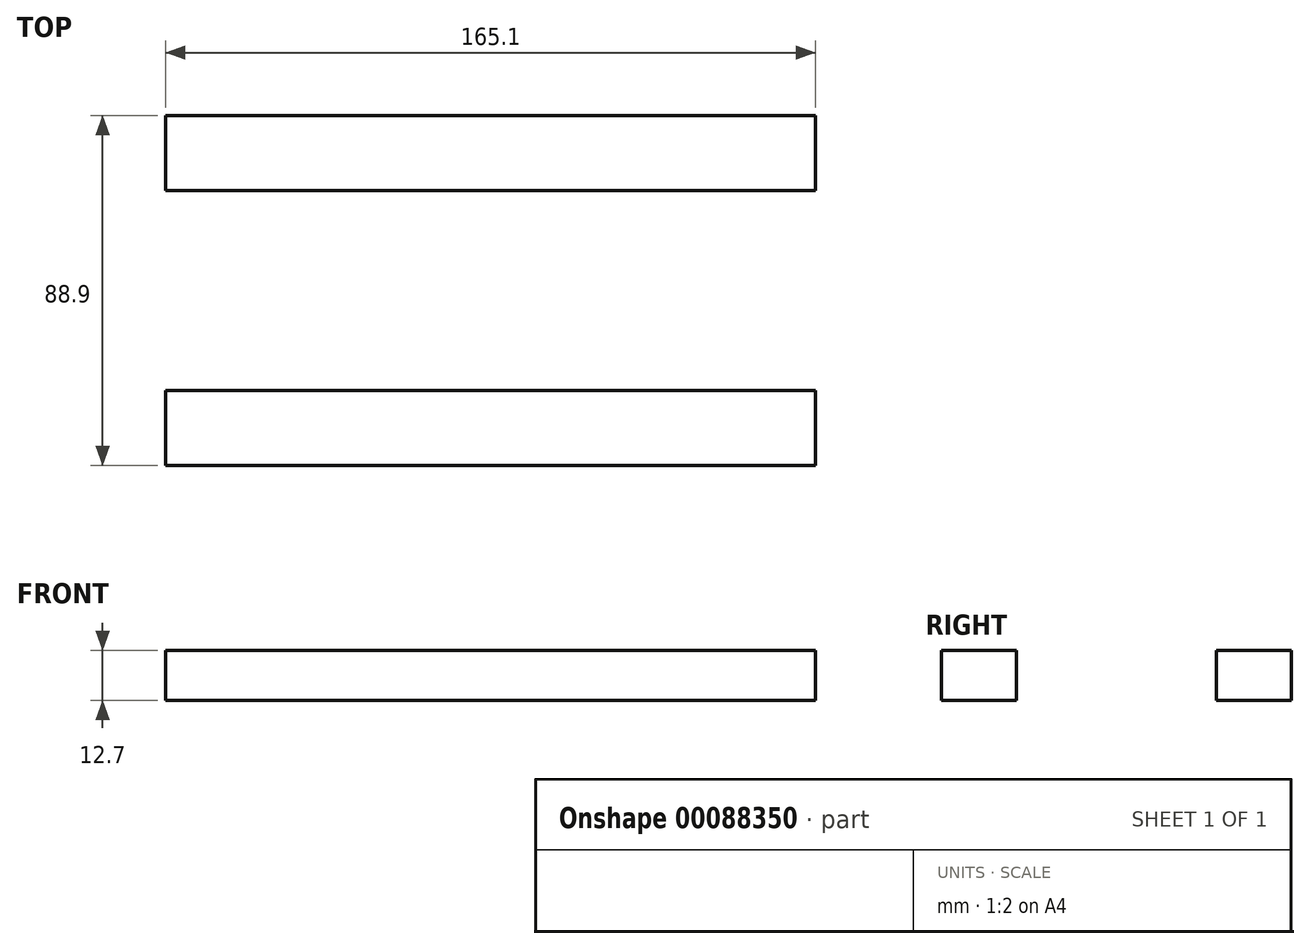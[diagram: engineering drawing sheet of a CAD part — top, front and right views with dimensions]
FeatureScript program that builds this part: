
annotation { "Feature Type Name" : "Feature", "Feature Type Description" : "" }
export const myFeature = defineFeature(function(context is Context, id is Id, definition is map)
    precondition{}
    {
        {
            var Q0;
            Q0=qCreatedBy(makeId("Right.planeOp"),FACE);
            var sketch = newSketch(context, id + "F0", { "sketchPlane" : qUnion([Q0])});
            skLineSegment(sketch, "E0.bottom", {"start": v(0, 0) * mm, "end": v(88.9, 0) * mm});
            skLineSegment(sketch, "E0.top", {"start": v(0, 44.45) * mm, "end": v(88.9, 44.45) * mm});
            skLineSegment(sketch, "E0.left", {"start": v(0, 0) * mm, "end": v(0, 44.45) * mm});
            skLineSegment(sketch, "E0.right", {"start": v(88.9, 0) * mm, "end": v(88.9, 44.45) * mm});
            skLineSegment(sketch, "E1.bottom", {"start": v(0, 44.45) * mm, "end": v(19.05, 44.45) * mm});
            skLineSegment(sketch, "E1.top", {"start": v(0, 31.75) * mm, "end": v(19.05, 31.75) * mm});
            skLineSegment(sketch, "E1.left", {"start": v(0, 44.45) * mm, "end": v(0, 31.75) * mm});
            skLineSegment(sketch, "E1.right", {"start": v(19.05, 44.45) * mm, "end": v(19.05, 31.75) * mm});
            skLineSegment(sketch, "E2.bottom", {"start": v(88.9, 44.45) * mm, "end": v(69.85, 44.45) * mm});
            skLineSegment(sketch, "E2.top", {"start": v(88.9, 31.75) * mm, "end": v(69.85, 31.75) * mm});
            skLineSegment(sketch, "E2.left", {"start": v(88.9, 44.45) * mm, "end": v(88.9, 31.75) * mm});
            skLineSegment(sketch, "E2.right", {"start": v(69.85, 44.45) * mm, "end": v(69.85, 31.75) * mm});
            skLineSegment(sketch, "E3", {"start": v(19.05, 31.75) * mm, "end": v(19.05, 0) * mm});
            skLineSegment(sketch, "E4", {"start": v(19.05, 0) * mm, "end": v(19.05, 12.7) * mm});
            skLineSegment(sketch, "E5", {"start": v(19.05, 12.7) * mm, "end": v(69.85, 12.7) * mm});
            skLineSegment(sketch, "E6", {"start": v(69.85, 12.7) * mm, "end": v(69.85, 31.75) * mm});
            skLineSegment(sketch, "E7", {"start": v(69.85, 0) * mm, "end": v(69.85, 12.7) * mm});
            skSolve(sketch);
        }
        {
            var Q0;
            {var subQ0=sQuery(id+"F0.wireOp",EDGE,"E0.left");Q0=makeQuery(id+"F0.imprint","IMPRINT",FACE,{"disambiguationData":[TD([[makeQuery(id+"F0.imprint","IMPRINT",EDGE,{"derivedFrom":subQ0}),-1.0]])]});}
            var Q1;
            Q1=makeQuery(id+"F0.imprint","IMPRINT",FACE,{"disambiguationData":[TD([[makeQuery(id+"F0.imprint","IMPRINT",EDGE,{"derivedFrom":sQuery(id+"F0.wireOp",EDGE,"E0.top")}),-1.0]])]});
            var Q2;
            {var subQ0=sQuery(id+"F0.wireOp",EDGE,"E0.right");Q2=makeQuery(id+"F0.imprint","IMPRINT",FACE,{"disambiguationData":[TD([[makeQuery(id+"F0.imprint","IMPRINT",EDGE,{"derivedFrom":subQ0}),1.0]])]});}
            extrude(context, id + "F1", {"entities" : qUnion([Q0, Q1, Q2]), "depth" : 165.1 * mm});
        }
        {
            var Q0;
            Q0=makeQuery(id+"F1.opExtrude","SWEPT_FACE",FACE,{"disambiguationData":[OSD([sQuery(id+"F0.wireOp",EDGE,"E0.top")])]});
            var sketch = newSketch(context, id + "F2", { "sketchPlane" : qUnion([Q0])});
            skLineSegment(sketch, "E8", {"start": v(0, 19.05) * mm, "end": v(0, 69.85) * mm});
            skLineSegment(sketch, "E9", {"start": v(0, 69.85) * mm, "end": v(0, 44.45) * mm});
            skLineSegment(sketch, "E10", {"start": v(0, 44.45) * mm, "end": v(35.05, 44.45) * mm});
            skLineSegment(sketch, "E11", {"start": v(35.05, 44.45) * mm, "end": v(130.3, 44.45) * mm});
            skSolve(sketch);
        }
        {
            var Q0;
            Q0=sQuery(id+"F2.wireOp",VERTEX,"E11.end");
            var Q1;
            Q1=sQuery(id+"F2.wireOp",VERTEX,"E11.start");
            var Q2;
            Q2=makeQuery(id+"F1.opExtrude","SWEPT_BODY",BODY,{"disambiguationData":[OSD([sQuery(id+"F0.wireOp",EDGE,"E0.bottom"),sQuery(id+"F0.wireOp",EDGE,"E0.top"),sQuery(id+"F0.wireOp",EDGE,"E0.left"),sQuery(id+"F0.wireOp",EDGE,"E0.right"),sQuery(id+"F0.wireOp",EDGE,"E1.top"),sQuery(id+"F0.wireOp",EDGE,"E1.right"),sQuery(id+"F0.wireOp",EDGE,"E2.top"),sQuery(id+"F0.wireOp",EDGE,"E2.right"),sQuery(id+"F0.wireOp",EDGE,"E4"),sQuery(id+"F0.wireOp",EDGE,"E5"),sQuery(id+"F0.wireOp",EDGE,"E7")])]});
            hole(context, id + "F3", {"style" : HoleStyle.SIMPLE, "endStyle" : HoleEndStyle.BLIND, "holeDiameter" : 25.4 * mm, "holeDepth" : 25.4 * mm, "locations" : qUnion([Q0, Q1]), "scope" : qUnion([Q2])});
        }
    });
